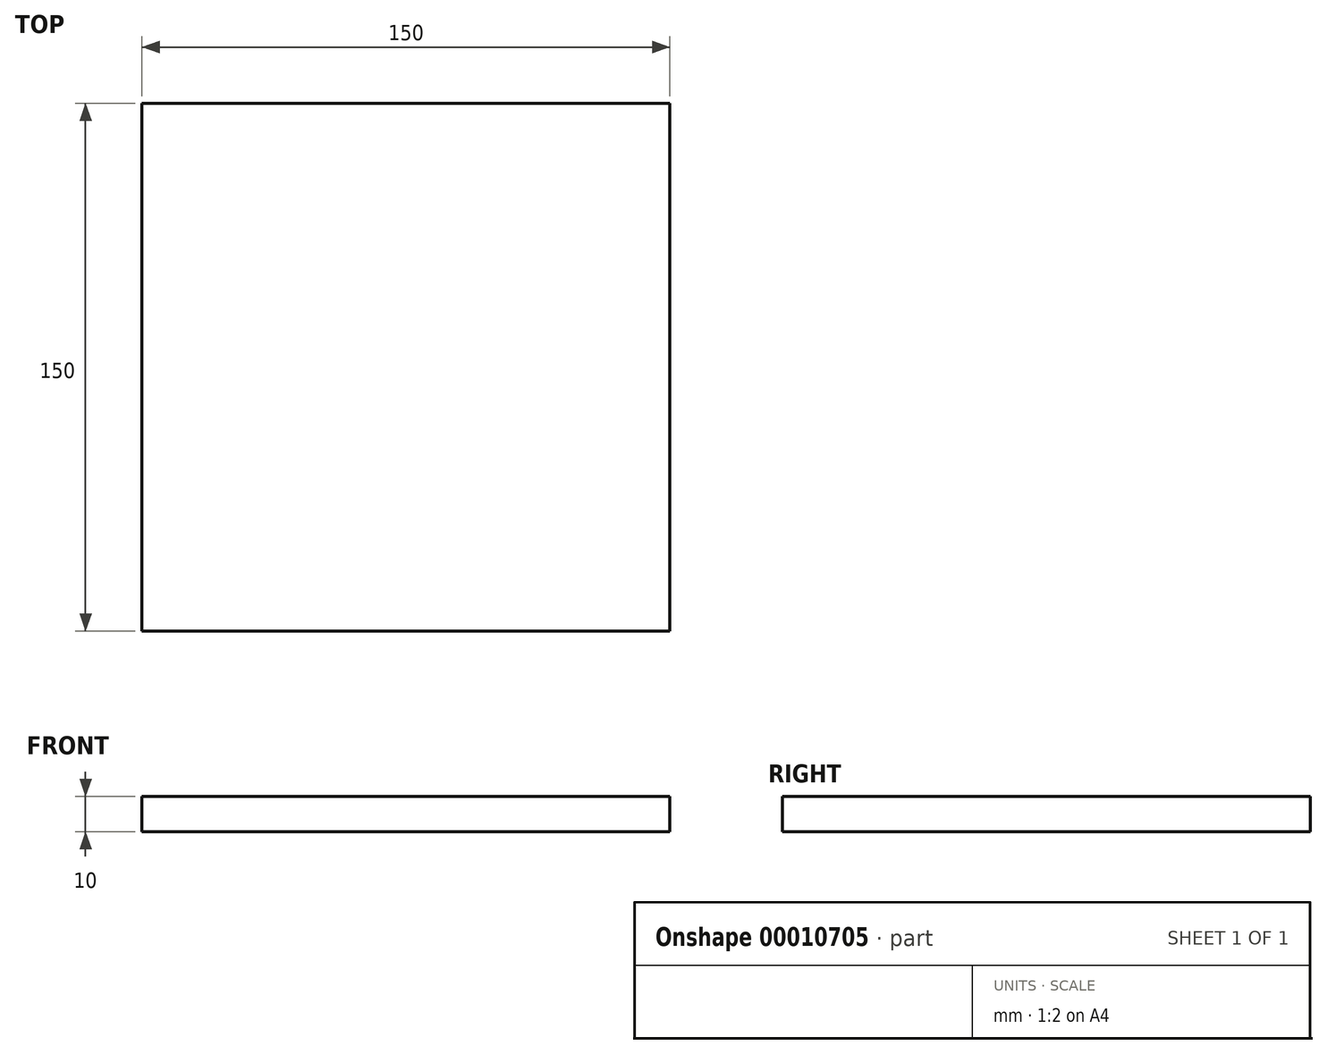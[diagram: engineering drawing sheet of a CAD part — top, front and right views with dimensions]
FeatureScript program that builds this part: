
annotation { "Feature Type Name" : "Feature", "Feature Type Description" : "" }
export const myFeature = defineFeature(function(context is Context, id is Id, definition is map)
    precondition{}
    {
        {
            var Q0;
            Q0=qCreatedBy(makeId("Top.planeOp"),FACE);
            var sketch = newSketch(context, id + "F1", { "sketchPlane" : qUnion([Q0])});
            skLineSegment(sketch, "E0.rect.bottom", {"start": v(75, 75) * mm, "end": v(-75, 75) * mm});
            skLineSegment(sketch, "E0.rect.top", {"start": v(75, -75) * mm, "end": v(-75, -75) * mm});
            skLineSegment(sketch, "E0.rect.left", {"start": v(75, 75) * mm, "end": v(75, -75) * mm});
            skLineSegment(sketch, "E0.rect.right", {"start": v(-75, 75) * mm, "end": v(-75, -75) * mm});
            skPoint(sketch, "E0.rect.middle", {"position": v(0, 0) * mm});
            skPoint(sketch, "E1.rect.top.start.orphan", {"position": v(75.55, -75.55) * mm});
            skPoint(sketch, "E1.rect.right.end.orphan", {"position": v(-75.55, -75.55) * mm});
            skPoint(sketch, "E1.rect.bottom.end.orphan", {"position": v(-75.55, 75.55) * mm});
            skPoint(sketch, "E1.rect.bottom.start.orphan", {"position": v(75.55, 75.55) * mm});
            skSolve(sketch);
        }
        {
            var Q0;
            Q0=makeQuery(id+"F1.imprint","IMPRINT",FACE,{"disambiguationData":[TD([[makeQuery(id+"F1.imprint","IMPRINT",EDGE,{"derivedFrom":sQuery(id+"F1.wireOp",EDGE,"E0.rect.bottom")}),1.0]])]});
            extrude(context, id + "F0", {"entities" : qUnion([Q0]), "depth" : 10 * mm});
        }
    });
